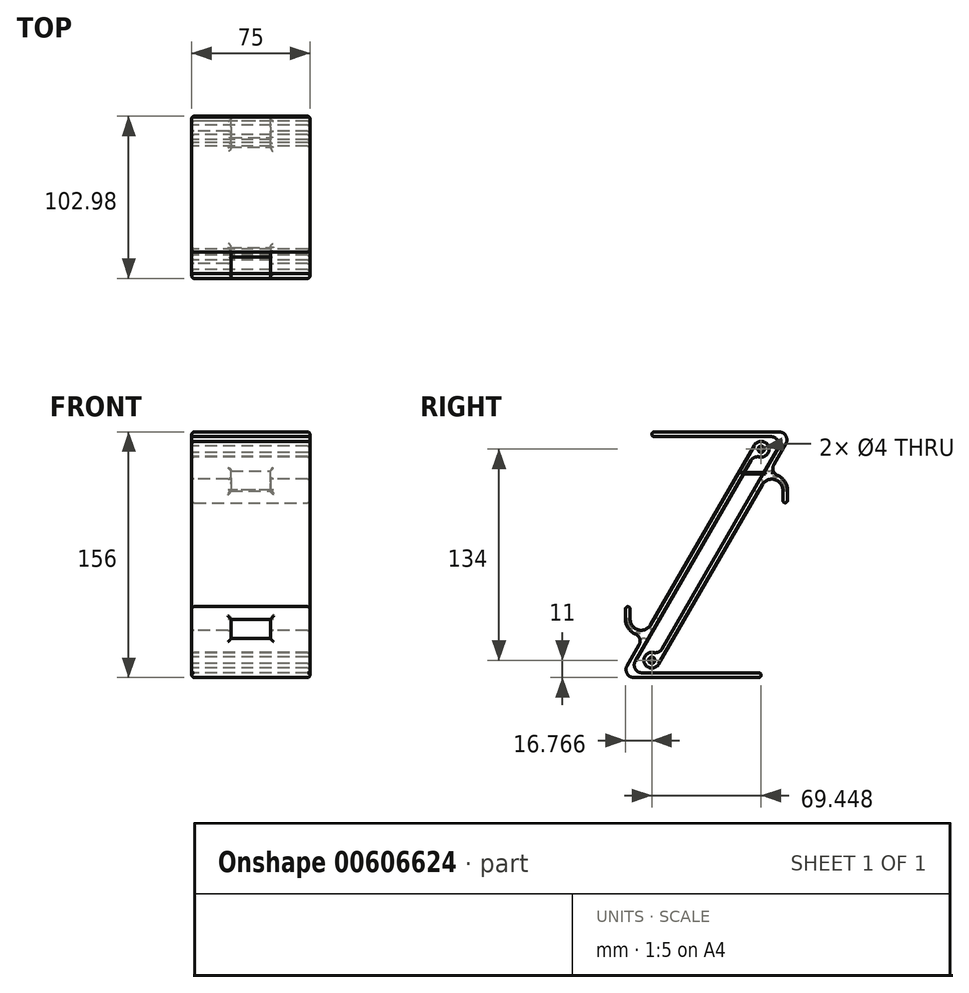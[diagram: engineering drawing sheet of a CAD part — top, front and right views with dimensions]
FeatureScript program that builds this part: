
annotation { "Feature Type Name" : "Feature", "Feature Type Description" : "" }
export const myFeature = defineFeature(function(context is Context, id is Id, definition is map)
    precondition{}
    {
        {
            var Q0;
            Q0=qCreatedBy(makeId("Right.planeOp"),FACE);
            var sketch = newSketch(context, id + "F0", { "sketchPlane" : qUnion([Q0])});
            skLineSegment(sketch, "E0.2", {"start": v(-43.49, -30) * mm, "end": v(-43.49, -38) * mm});
            skArc(sketch, "E0.4", {"start": v(-43.49, -38) * mm, "mid": v(-41.8, -43.57) * mm, "end": v(-37.29, -47.25) * mm});
            skLineSegment(sketch, "E1.2", {"start": v(-40.49, -30) * mm, "end": v(-40.49, -38) * mm});
            skLineSegment(sketch, "E1.3", {"start": v(-27.42, -41.5) * mm, "end": v(38.4, 72.5) * mm});
            skArc(sketch, "E2.filletArc", {"start": v(-40.49, -38) * mm, "mid": v(-35.3, -44.76) * mm, "end": v(-27.42, -41.5) * mm});
            skLineSegment(sketch, "E3", {"start": v(-43.49, -30) * mm, "end": v(-40.49, -30) * mm});
            skLineSegment(sketch, "E4", {"start": v(-42.44, -67.5) * mm, "end": v(-34.86, -54.37) * mm});
            skLineSegment(sketch, "E5.bottom", {"start": v(-38.1, -75) * mm, "end": v(42.72, -75) * mm});
            skLineSegment(sketch, "E5.top", {"start": v(-32.9, -72) * mm, "end": v(42.72, -72) * mm});
            skLineSegment(sketch, "E5.right", {"start": v(42.72, -75) * mm, "end": v(42.72, -72) * mm});
            skLineSegment(sketch, "E6", {"start": v(-37.24, -64.5) * mm, "end": v(36.22, 62.74) * mm});
            skPoint(sketch, "E7", {"position": v(0, 0) * mm});
            skArc(sketch, "E8", {"start": v(38.4, 72.5) * mm, "mid": v(47.3, 72.01) * mm, "end": v(41.64, 65.12) * mm});
            skPoint(sketch, "E9.visualSharp", {"position": v(-31, -47.68) * mm});
            skArc(sketch, "E9.filletArc", {"start": v(-34.86, -54.37) * mm, "mid": v(-34.45, -50.26) * mm, "end": v(-37.29, -47.25) * mm});
            skArc(sketch, "E10.filletArc", {"start": v(-37.24, -64.5) * mm, "mid": v(-37.24, -69.5) * mm, "end": v(-32.9, -72) * mm});
            skArc(sketch, "E11.filletArc", {"start": v(-42.44, -67.5) * mm, "mid": v(-42.44, -72.5) * mm, "end": v(-38.1, -75) * mm});
            skArc(sketch, "E12", {"start": v(41.64, 65.12) * mm, "mid": v(38.54, 64.82) * mm, "end": v(36.22, 62.74) * mm});
            skCircle(sketch, "E13", {"center": v(42.72, 70) * mm, "radius": 2 * mm});
            skSolve(sketch);
        }
        {
            var Q0;
            Q0=qSketchRegion(id+"F0",true);
            extrude(context, id + "F1", {"entities" : qUnion([Q0]), "endBound" : BoundingType.SYMMETRIC, "depth" : 75 * mm, "offsetDistance" : 25 * mm});
        }
        {
            var Q0;
            Q0=makeQuery(id+"F1.opExtrude","SWEPT_FACE",FACE,{"disambiguationData":[OSD([sQuery(id+"F0.wireOp",EDGE,"E0.2")])]});
            var sketch = newSketch(context, id + "F2", { "sketchPlane" : qUnion([Q0])});
            skLineSegment(sketch, "E14.bottom", {"start": v(-12.5, -38) * mm, "end": v(12.5, -38) * mm});
            skLineSegment(sketch, "E14.top", {"start": v(-12.5, -50.25) * mm, "end": v(12.5, -50.25) * mm});
            skLineSegment(sketch, "E14.left", {"start": v(-12.5, -38) * mm, "end": v(-12.5, -50.25) * mm});
            skLineSegment(sketch, "E14.right", {"start": v(12.5, -38) * mm, "end": v(12.5, -50.25) * mm});
            skSolve(sketch);
        }
        {
            var Q0;
            Q0=qSketchRegion(id+"F2",true);
            extrude(context, id + "F3", {"entities" : qUnion([Q0]), "operationType" : NewBodyOperationType.REMOVE, "oppositeDirection" : true, "depth" : 25 * mm, "offsetDistance" : 25 * mm});
        }
        {
            var Q0;
            Q0=makeQuery(id+"F1.opExtrude","SWEPT_FACE",FACE,{"disambiguationData":[OSD([sQuery(id+"F0.wireOp",EDGE,"E3")])]});
            var Q1;
            Q1=makeQuery(id+"F1.opExtrude","CAP_FACE",FACE,{"disambiguationData":[OSD([sQuery(id+"F0.wireOp",EDGE,"E0.2"),sQuery(id+"F0.wireOp",EDGE,"E0.4"),sQuery(id+"F0.wireOp",EDGE,"E1.2"),sQuery(id+"F0.wireOp",EDGE,"E1.3"),sQuery(id+"F0.wireOp",EDGE,"E2.filletArc"),sQuery(id+"F0.wireOp",EDGE,"E3"),sQuery(id+"F0.wireOp",EDGE,"OJqH4mra-1SRE-s8op-VV3v-gDYp8EEXXtRn"),sQuery(id+"F0.wireOp",EDGE,"E4"),sQuery(id+"F0.wireOp",EDGE,"E5.bottom"),sQuery(id+"F0.wireOp",EDGE,"E5.top"),sQuery(id+"F0.wireOp",EDGE,"E5.right"),sQuery(id+"F0.wireOp",EDGE,"E6"),sQuery(id+"F0.wireOp",EDGE,"E8"),sQuery(id+"F0.wireOp",EDGE,"jVerfQlz-GGoS-WxWe-SnGt-XEWwIJdHr9bm"),sQuery(id+"F0.wireOp",EDGE,"E9.filletArc"),sQuery(id+"F0.wireOp",EDGE,"E10.filletArc"),sQuery(id+"F0.wireOp",EDGE,"E11.filletArc")])],"isStart":false});
            var Q2;
            Q2=makeQuery(id+"F1.opExtrude","CAP_FACE",FACE,{"disambiguationData":[OSD([sQuery(id+"F0.wireOp",EDGE,"E0.2"),sQuery(id+"F0.wireOp",EDGE,"E0.4"),sQuery(id+"F0.wireOp",EDGE,"E1.2"),sQuery(id+"F0.wireOp",EDGE,"E1.3"),sQuery(id+"F0.wireOp",EDGE,"E2.filletArc"),sQuery(id+"F0.wireOp",EDGE,"E3"),sQuery(id+"F0.wireOp",EDGE,"OJqH4mra-1SRE-s8op-VV3v-gDYp8EEXXtRn"),sQuery(id+"F0.wireOp",EDGE,"E4"),sQuery(id+"F0.wireOp",EDGE,"E5.bottom"),sQuery(id+"F0.wireOp",EDGE,"E5.top"),sQuery(id+"F0.wireOp",EDGE,"E5.right"),sQuery(id+"F0.wireOp",EDGE,"E6"),sQuery(id+"F0.wireOp",EDGE,"E8"),sQuery(id+"F0.wireOp",EDGE,"jVerfQlz-GGoS-WxWe-SnGt-XEWwIJdHr9bm"),sQuery(id+"F0.wireOp",EDGE,"E9.filletArc"),sQuery(id+"F0.wireOp",EDGE,"E10.filletArc"),sQuery(id+"F0.wireOp",EDGE,"E11.filletArc")])],"isStart":true});
            var Q3;
            Q3=makeQuery(id+"F1.opExtrude","SWEPT_FACE",FACE,{"disambiguationData":[OSD([sQuery(id+"F0.wireOp",EDGE,"E5.right")])]});
            var Q4;
            Q4=makeQuery(id+"F1.opExtrude","SWEPT_EDGE",EDGE,{"disambiguationData":[OSD([sQuery(id+"F0.wireOp",EDGE,"OJqH4mra-1SRE-s8op-VV3v-gDYp8EEXXtRn"),sQuery(id+"F0.wireOp",EDGE,"E8")])]});
            var Q5;
            Q5=makeQuery(id+"F1.opExtrude","SWEPT_EDGE",EDGE,{"disambiguationData":[OSD([sQuery(id+"F0.wireOp",EDGE,"OJqH4mra-1SRE-s8op-VV3v-gDYp8EEXXtRn"),sQuery(id+"F0.wireOp",EDGE,"jVerfQlz-GGoS-WxWe-SnGt-XEWwIJdHr9bm")])]});
            fillet(context, id + "F4", {"entities" : qUnion([Q0, Q1, Q2, Q3, Q4, Q5]), "radius" : 1.5 * mm, "tangentPropagation" : true, "allowEdgeOverflow" : false});
        }
        {
            var Q0;
            Q0=makeQuery(id+"F3.boolean.opBoolean","INTERSECT",EDGE,{"derivedFrom":[makeQuery(id+"F1.opExtrude","SWEPT_FACE",FACE,{"disambiguationData":[OSD([sQuery(id+"F0.wireOp",EDGE,"E9.filletArc")])]}),makeQuery(id+"F3.opExtrude","SWEPT_FACE",FACE,{"disambiguationData":[OSD([sQuery(id+"F2.wireOp",EDGE,"E14.top")])]})]});
            var Q1;
            Q1=makeQuery(id+"F3.boolean.opBoolean","INTERSECT",EDGE,{"derivedFrom":[makeQuery(id+"F1.opExtrude","SWEPT_FACE",FACE,{"disambiguationData":[OSD([sQuery(id+"F0.wireOp",EDGE,"E0.4")])]}),makeQuery(id+"F3.opExtrude","SWEPT_FACE",FACE,{"disambiguationData":[OSD([sQuery(id+"F2.wireOp",EDGE,"E14.right")])]})]});
            var Q2;
            Q2=makeQuery(id+"F3.boolean.opBoolean","INTERSECT",EDGE,{"derivedFrom":[makeQuery(id+"F1.opExtrude","SWEPT_FACE",FACE,{"disambiguationData":[OSD([sQuery(id+"F0.wireOp",EDGE,"E0.4")])]}),makeQuery(id+"F3.opExtrude","SWEPT_FACE",FACE,{"disambiguationData":[OSD([sQuery(id+"F2.wireOp",EDGE,"E14.left")])]})]});
            var Q3;
            Q3=makeQuery(id+"F3.boolean.opBoolean","MERGE",EDGE,{"derivedFrom":[makeQuery(id+"F1.opExtrude","SWEPT_EDGE",EDGE,{"disambiguationData":[OSD([sQuery(id+"F0.wireOp",EDGE,"E0.2"),sQuery(id+"F0.wireOp",EDGE,"E0.4")])]}),makeQuery(id+"F3.opExtrude","CAP_EDGE",EDGE,{"disambiguationData":[OSD([sQuery(id+"F2.wireOp",EDGE,"E14.bottom")])],"isStart":true})]});
            fillet(context, id + "F5", {"entities" : qUnion([Q0, Q1, Q2, Q3]), "radius" : 2 * mm, "tangentPropagation" : true, "allowEdgeOverflow" : false});
        }
        {
            var Q0;
            Q0=makeQuery(id+"F3.boolean.opBoolean","INTERSECT",EDGE,{"derivedFrom":[makeQuery(id+"F1.opExtrude","SWEPT_FACE",FACE,{"disambiguationData":[OSD([sQuery(id+"F0.wireOp",EDGE,"E1.3")])]}),makeQuery(id+"F3.opExtrude","SWEPT_FACE",FACE,{"disambiguationData":[OSD([sQuery(id+"F2.wireOp",EDGE,"E14.bottom")])]})]});
            var Q1;
            Q1=makeQuery(id+"F3.boolean.opBoolean","INTERSECT",EDGE,{"derivedFrom":[makeQuery(id+"F1.opExtrude","SWEPT_FACE",FACE,{"disambiguationData":[OSD([sQuery(id+"F0.wireOp",EDGE,"E2.filletArc")])]}),makeQuery(id+"F3.opExtrude","SWEPT_FACE",FACE,{"disambiguationData":[OSD([sQuery(id+"F2.wireOp",EDGE,"E14.left")])]})]});
            var Q2;
            Q2=makeQuery(id+"F3.boolean.opBoolean","INTERSECT",EDGE,{"derivedFrom":[makeQuery(id+"F1.opExtrude","SWEPT_FACE",FACE,{"disambiguationData":[OSD([sQuery(id+"F0.wireOp",EDGE,"E2.filletArc")])]}),makeQuery(id+"F3.opExtrude","SWEPT_FACE",FACE,{"disambiguationData":[OSD([sQuery(id+"F2.wireOp",EDGE,"E14.right")])]})]});
            fillet(context, id + "F6", {"entities" : qUnion([Q0, Q1, Q2]), "radius" : 2 * mm, "tangentPropagation" : true, "allowEdgeOverflow" : false});
        }
        {
            var Q0;
            Q0=makeQuery(id+"F3.boolean.opBoolean","INTERSECT",EDGE,{"derivedFrom":[makeQuery(id+"F1.opExtrude","SWEPT_FACE",FACE,{"disambiguationData":[OSD([sQuery(id+"F0.wireOp",EDGE,"E6")])]}),makeQuery(id+"F3.opExtrude","SWEPT_FACE",FACE,{"disambiguationData":[OSD([sQuery(id+"F2.wireOp",EDGE,"E14.right")])]})]});
            var Q1;
            Q1=makeQuery(id+"F3.boolean.opBoolean","INTERSECT",EDGE,{"derivedFrom":[makeQuery(id+"F1.opExtrude","SWEPT_FACE",FACE,{"disambiguationData":[OSD([sQuery(id+"F0.wireOp",EDGE,"E6")])]}),makeQuery(id+"F3.opExtrude","SWEPT_FACE",FACE,{"disambiguationData":[OSD([sQuery(id+"F2.wireOp",EDGE,"E14.top")])]})]});
            var Q2;
            Q2=makeQuery(id+"F6.opFillet","BLEND_EDGE",EDGE,{"blendedFrom":[makeQuery(id+"F3.boolean.opBoolean","INTERSECT",EDGE,{"derivedFrom":[makeQuery(id+"F1.opExtrude","SWEPT_FACE",FACE,{"disambiguationData":[OSD([sQuery(id+"F0.wireOp",EDGE,"E1.3")])]}),makeQuery(id+"F3.opExtrude","SWEPT_FACE",FACE,{"disambiguationData":[OSD([sQuery(id+"F2.wireOp",EDGE,"E14.bottom")])]})]}),makeQuery(id+"F1.opExtrude","SWEPT_FACE",FACE,{"disambiguationData":[OSD([sQuery(id+"F0.wireOp",EDGE,"E6")])]})],"blendedInto":[makeQuery(id+"F1.opExtrude","SWEPT_FACE",FACE,{"disambiguationData":[OSD([sQuery(id+"F0.wireOp",EDGE,"E6")])]})]});
            var Q3;
            Q3=makeQuery(id+"F3.boolean.opBoolean","INTERSECT",EDGE,{"derivedFrom":[makeQuery(id+"F1.opExtrude","SWEPT_FACE",FACE,{"disambiguationData":[OSD([sQuery(id+"F0.wireOp",EDGE,"E6")])]}),makeQuery(id+"F3.opExtrude","SWEPT_FACE",FACE,{"disambiguationData":[OSD([sQuery(id+"F2.wireOp",EDGE,"E14.left")])]})]});
            fillet(context, id + "F7", {"entities" : qUnion([Q0, Q1, Q2, Q3]), "radius" : 1.4 * mm, "tangentPropagation" : true, "allowEdgeOverflow" : false});
        }
        {
            var Q0;
            Q0=qCreatedBy(makeId("Front.planeOp"),FACE);
            cPlane(context, id + "F8", {"entities" : qUnion([Q0]), "cplaneType" : CPlaneType.OFFSET, "offset" : 8 * mm, "oppositeDirection" : true, "width" : 150 * mm, "height" : 150 * mm});
        }
        {
            var Q0;
            Q0=qCreatedBy(id+"F8.planeOp",FACE);
            var sketch = newSketch(context, id + "F9", { "sketchPlane" : qUnion([Q0])});
            skLineSegment(sketch, "E15", {"start": v(0, 3) * mm, "end": v(46.47, 3) * mm, "construction": true});
            skSolve(sketch);
        }
        {
            var Q0;
            Q0=makeQuery(id+"F1.opExtrude","SWEPT_BODY",BODY,{"disambiguationData":[OSD([sQuery(id+"F0.wireOp",EDGE,"E0.2"),sQuery(id+"F0.wireOp",EDGE,"E0.4"),sQuery(id+"F0.wireOp",EDGE,"E1.2"),sQuery(id+"F0.wireOp",EDGE,"E1.3"),sQuery(id+"F0.wireOp",EDGE,"E2.filletArc"),sQuery(id+"F0.wireOp",EDGE,"E3"),sQuery(id+"F0.wireOp",EDGE,"E4"),sQuery(id+"F0.wireOp",EDGE,"E5.bottom"),sQuery(id+"F0.wireOp",EDGE,"E5.top"),sQuery(id+"F0.wireOp",EDGE,"E5.right"),sQuery(id+"F0.wireOp",EDGE,"E6"),sQuery(id+"F0.wireOp",EDGE,"E8"),sQuery(id+"F0.wireOp",EDGE,"E9.filletArc"),sQuery(id+"F0.wireOp",EDGE,"E10.filletArc"),sQuery(id+"F0.wireOp",EDGE,"E11.filletArc"),sQuery(id+"F0.wireOp",EDGE,"E12"),sQuery(id+"F0.wireOp",EDGE,"E13")])]});
            var Q1;
            Q1=sQuery(id+"F9.wireOp",EDGE,"E15");
            circularPattern(context, id + "F10", {"entities" : qUnion([Q0]), "axis" : qUnion([Q1]), "angle" : 360 * degree, "instanceCount" : 2, "equalSpace" : true});
        }
        {
            var Q0;
            Q0=makeQuery(id+"F10.opPattern","COPY",FACE,{"derivedFrom":makeQuery(id+"F4.opFillet","SPLIT",FACE,{"disambiguationData":[OD(1.0)],"derivedFrom":makeQuery(id+"F1.opExtrude","CAP_FACE",FACE,{"disambiguationData":[OSD([sQuery(id+"F0.wireOp",EDGE,"E0.2"),sQuery(id+"F0.wireOp",EDGE,"E0.4"),sQuery(id+"F0.wireOp",EDGE,"E1.2"),sQuery(id+"F0.wireOp",EDGE,"E1.3"),sQuery(id+"F0.wireOp",EDGE,"E2.filletArc"),sQuery(id+"F0.wireOp",EDGE,"E3"),sQuery(id+"F0.wireOp",EDGE,"E4"),sQuery(id+"F0.wireOp",EDGE,"E5.bottom"),sQuery(id+"F0.wireOp",EDGE,"E5.top"),sQuery(id+"F0.wireOp",EDGE,"E5.right"),sQuery(id+"F0.wireOp",EDGE,"E6"),sQuery(id+"F0.wireOp",EDGE,"E8"),sQuery(id+"F0.wireOp",EDGE,"E9.filletArc"),sQuery(id+"F0.wireOp",EDGE,"E10.filletArc"),sQuery(id+"F0.wireOp",EDGE,"E11.filletArc"),sQuery(id+"F0.wireOp",EDGE,"E12"),sQuery(id+"F0.wireOp",EDGE,"E13")])],"isStart":false})}),"instanceName":"1"});
            var sketch = newSketch(context, id + "F11", { "sketchPlane" : qUnion([Q0])});
            skLineSegment(sketch, "E16.bottom", {"start": v(29.76, 55.26) * mm, "end": v(49.76, 55.26) * mm});
            skLineSegment(sketch, "E16.top", {"start": v(29.76, 54.26) * mm, "end": v(49.76, 54.26) * mm});
            skLineSegment(sketch, "E16.left", {"start": v(29.76, 55.26) * mm, "end": v(29.76, 54.26) * mm});
            skLineSegment(sketch, "E16.right", {"start": v(49.76, 55.26) * mm, "end": v(49.76, 54.26) * mm});
            skSolve(sketch);
        }
        {
            var Q0;
            Q0 = qSketchRegion(id + "F11", true);
            extrude(context, id + "F12", {"entities" : qUnion([Q0]), "operationType" : NewBodyOperationType.ADD, "oppositeDirection" : true, "depth" : 0.01 * mm, "offsetDistance" : 25 * mm});
        }
    });
